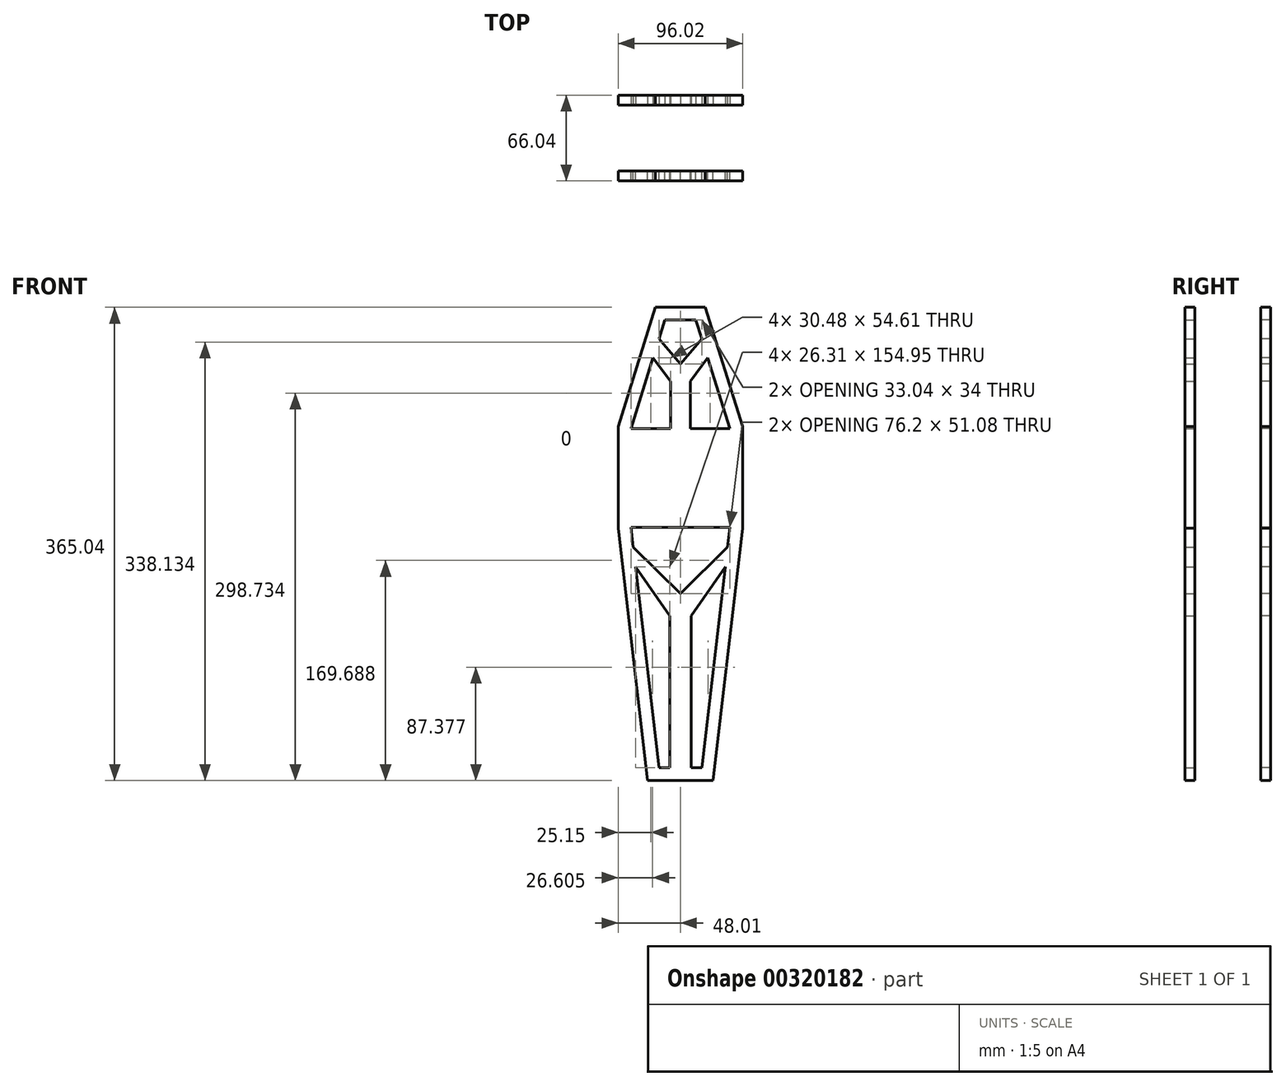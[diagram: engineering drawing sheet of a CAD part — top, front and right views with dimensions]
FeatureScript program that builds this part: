
annotation { "Feature Type Name" : "Feature", "Feature Type Description" : "" }
export const myFeature = defineFeature(function(context is Context, id is Id, definition is map)
    precondition{}
    {
        {
            var Q0;
            Q0=qCreatedBy(makeId("Front.planeOp"),FACE);
            var sketch = newSketch(context, id + "F0", { "sketchPlane" : qUnion([Q0])});
            skLineSegment(sketch, "E0.bottom", {"start": v(-38.1, 0) * mm, "end": v(38.1, 0) * mm});
            skLineSegment(sketch, "E0.top", {"start": v(-38.1, -76.2) * mm, "end": v(38.1, -76.2) * mm});
            skLineSegment(sketch, "E0.left", {"start": v(-38.1, 0) * mm, "end": v(-38.1, -76.2) * mm});
            skLineSegment(sketch, "E0.right", {"start": v(38.1, 0) * mm, "end": v(38.1, -76.2) * mm});
            skLineSegment(sketch, "E1", {"start": v(0, -38.1) * mm, "end": v(0, 83.7) * mm, "construction": true});
            skPoint(sketch, "E1.startSnap0", {"position": v(0, -76.2) * mm});
            skPoint(sketch, "E1.startSnap1", {"position": v(-38.1, -38.1) * mm});
            skPoint(sketch, "E1.endSnap0", {"position": v(0, 0) * mm});
            skLineSegment(sketch, "E2", {"start": v(0, 83.7) * mm, "end": v(-11.98, 83.7) * mm});
            skLineSegment(sketch, "E3", {"start": v(-11.98, 83.7) * mm, "end": v(0, 83.7) * mm});
            skLineSegment(sketch, "E4", {"start": v(11.98, 83.7) * mm, "end": v(0, 83.7) * mm});
            skLineSegment(sketch, "E5", {"start": v(-38.1, 0) * mm, "end": v(-11.98, 83.7) * mm});
            skLineSegment(sketch, "E6", {"start": v(38.1, 0) * mm, "end": v(11.98, 83.7) * mm});
            skLineSegment(sketch, "E7", {"start": v(0, -38.1) * mm, "end": v(0, -261.53) * mm, "construction": true});
            skLineSegment(sketch, "E8", {"start": v(0, -261.53) * mm, "end": v(-16.5, -261.53) * mm});
            skLineSegment(sketch, "E9", {"start": v(0, -261.53) * mm, "end": v(16.5, -261.53) * mm});
            skLineSegment(sketch, "E10", {"start": v(-16.5, -261.53) * mm, "end": v(-38.1, -76.2) * mm});
            skLineSegment(sketch, "E11", {"start": v(16.5, -261.53) * mm, "end": v(38.1, -76.2) * mm});
            skLineSegment(sketch, "E12", {"start": v(-7.62, 0) * mm, "end": v(-7.62, 36.5) * mm});
            skLineSegment(sketch, "E13", {"start": v(7.62, 0) * mm, "end": v(7.62, 36.5) * mm});
            skLineSegment(sketch, "E14", {"start": v(16.52, 69.16) * mm, "end": v(0, 49.7) * mm});
            skLineSegment(sketch, "E15", {"start": v(21.06, 54.6) * mm, "end": v(7.62, 36.5) * mm});
            skLineSegment(sketch, "E16", {"start": v(-21.06, 54.6) * mm, "end": v(-7.62, 36.5) * mm});
            skLineSegment(sketch, "E17", {"start": v(-16.52, 69.16) * mm, "end": v(0, 49.7) * mm});
            skLineSegment(sketch, "E18", {"start": v(0, 49.7) * mm, "end": v(-7.62, 36.5) * mm});
            skLineSegment(sketch, "E19", {"start": v(0, 49.7) * mm, "end": v(7.62, 36.5) * mm});
            skLineSegment(sketch, "E20", {"start": v(-7.62, 36.5) * mm, "end": v(7.62, 36.5) * mm});
            skLineSegment(sketch, "E21", {"start": v(-36.32, -91.44) * mm, "end": v(0, -127.28) * mm});
            skLineSegment(sketch, "E22", {"start": v(-34.56, -106.58) * mm, "end": v(-8.25, -144.45) * mm});
            skLineSegment(sketch, "E23", {"start": v(36.32, -91.44) * mm, "end": v(0, -127.28) * mm});
            skLineSegment(sketch, "E24", {"start": v(34.56, -106.58) * mm, "end": v(8.25, -144.45) * mm});
            skLineSegment(sketch, "E25", {"start": v(-8.25, -261.53) * mm, "end": v(-8.25, -144.45) * mm});
            skLineSegment(sketch, "E26", {"start": v(8.25, -261.53) * mm, "end": v(8.25, -144.45) * mm});
            skLineSegment(sketch, "E27", {"start": v(-8.25, -144.45) * mm, "end": v(0, -127.28) * mm});
            skLineSegment(sketch, "E28", {"start": v(0, -127.28) * mm, "end": v(8.25, -144.45) * mm});
            skLineSegment(sketch, "E29", {"start": v(-8.25, -144.45) * mm, "end": v(8.25, -144.45) * mm});
            skLineSegment(sketch, "E30.0", {"start": v(-48, 1.5) * mm, "end": v(-48, -76.78) * mm});
            skLineSegment(sketch, "E30.1", {"start": v(-25.32, -271.43) * mm, "end": v(-48, -76.78) * mm});
            skLineSegment(sketch, "E30.2", {"start": v(-48, 1.5) * mm, "end": v(-19.27, 93.61) * mm});
            skLineSegment(sketch, "E30.3", {"start": v(0, -271.43) * mm, "end": v(-25.32, -271.43) * mm});
            skLineSegment(sketch, "E30.4", {"start": v(0, -271.43) * mm, "end": v(25.32, -271.43) * mm});
            skLineSegment(sketch, "E30.5", {"start": v(25.32, -271.43) * mm, "end": v(48, -76.78) * mm});
            skLineSegment(sketch, "E30.6", {"start": v(-19.27, 93.61) * mm, "end": v(0, 93.61) * mm});
            skLineSegment(sketch, "E30.7", {"start": v(19.27, 93.61) * mm, "end": v(0, 93.61) * mm});
            skLineSegment(sketch, "E30.8", {"start": v(48, 1.5) * mm, "end": v(19.27, 93.61) * mm});
            skLineSegment(sketch, "E30.9", {"start": v(48, 1.5) * mm, "end": v(48, -76.78) * mm});
            skSolve(sketch);
        }
        {
            var Q0;
            Q0=qCreatedBy(makeId("Front.planeOp"),FACE);
            cPlane(context, id + "F1", {"entities" : qUnion([Q0]), "cplaneType" : CPlaneType.OFFSET, "offset" : 25.4 * mm, "oppositeDirection" : true, "width" : 152.4 * mm, "height" : 152.4 * mm});
        }
        {
            var Q0;
            Q0=makeQuery(id+"F0.imprint","IMPRINT",FACE,{"disambiguationData":[TD([[makeQuery(id+"F0.imprint","IMPRINT",EDGE,{"derivedFrom":sQuery(id+"F0.wireOp",EDGE,"E18")}),1.0]])]});
            var Q1;
            {var subQ0=sQuery(id+"F0.wireOp",EDGE,"E12");Q1=makeQuery(id+"F0.imprint","IMPRINT",FACE,{"disambiguationData":[TD([[makeQuery(id+"F0.imprint","IMPRINT",EDGE,{"derivedFrom":subQ0}),-1.0]])]});}
            var Q2;
            {var subQ0=sQuery(id+"F0.wireOp",EDGE,"E14");Q2=makeQuery(id+"F0.imprint","IMPRINT",FACE,{"disambiguationData":[TD([[makeQuery(id+"F0.imprint","IMPRINT",EDGE,{"derivedFrom":subQ0}),1.0]])]});}
            var Q3;
            {var subQ0=sQuery(id+"F0.wireOp",EDGE,"E16");Q3=makeQuery(id+"F0.imprint","IMPRINT",FACE,{"disambiguationData":[TD([[makeQuery(id+"F0.imprint","IMPRINT",EDGE,{"derivedFrom":subQ0}),1.0]])]});}
            var Q4;
            {var subQ8=sQuery(id+"F0.wireOp",EDGE,"E0.left");Q4=makeQuery(id+"F0.imprint","IMPRINT",FACE,{"disambiguationData":[TD([[makeQuery(id+"F0.imprint","IMPRINT",EDGE,{"derivedFrom":subQ8}),-1.0]])]});}
            var Q5;
            Q5=makeQuery(id+"F0.imprint","IMPRINT",FACE,{"disambiguationData":[TD([[makeQuery(id+"F0.imprint","IMPRINT",EDGE,{"derivedFrom":sQuery(id+"F0.wireOp",EDGE,"E0.top")}),1.0]])]});
            var Q6;
            {var subQ0=sQuery(id+"F0.wireOp",EDGE,"E21");Q6=makeQuery(id+"F0.imprint","IMPRINT",FACE,{"disambiguationData":[TD([[makeQuery(id+"F0.imprint","IMPRINT",EDGE,{"derivedFrom":subQ0}),-1.0]])]});}
            var Q7;
            {var subQ0=sQuery(id+"F0.wireOp",EDGE,"E23");Q7=makeQuery(id+"F0.imprint","IMPRINT",FACE,{"disambiguationData":[TD([[makeQuery(id+"F0.imprint","IMPRINT",EDGE,{"derivedFrom":subQ0}),1.0]])]});}
            var Q8;
            Q8=makeQuery(id+"F0.imprint","IMPRINT",FACE,{"disambiguationData":[TD([[makeQuery(id+"F0.imprint","IMPRINT",EDGE,{"derivedFrom":sQuery(id+"F0.wireOp",EDGE,"E27")}),-1.0]])]});
            var Q9;
            {var subQ4=sQuery(id+"F0.wireOp",EDGE,"E25");Q9=makeQuery(id+"F0.imprint","IMPRINT",FACE,{"disambiguationData":[TD([[makeQuery(id+"F0.imprint","IMPRINT",EDGE,{"derivedFrom":subQ4}),-1.0]])]});}
            extrude(context, id + "F2", {"entities" : qUnion([Q0, Q1, Q2, Q3, Q4, Q5, Q6, Q7, Q8, Q9]), "depth" : 7.62 * mm});
        }
        {
            var Q0;
            Q0=makeQuery(id+"F2.opExtrude","SWEPT_BODY",BODY,{"disambiguationData":[OSD([sQuery(id+"F0.wireOp",EDGE,"E0.bottom"),sQuery(id+"F0.wireOp",EDGE,"E0.top"),sQuery(id+"F0.wireOp",EDGE,"E3"),sQuery(id+"F0.wireOp",EDGE,"E4"),sQuery(id+"F0.wireOp",EDGE,"E5"),sQuery(id+"F0.wireOp",EDGE,"E6"),sQuery(id+"F0.wireOp",EDGE,"E8"),sQuery(id+"F0.wireOp",EDGE,"E9"),sQuery(id+"F0.wireOp",EDGE,"E10"),sQuery(id+"F0.wireOp",EDGE,"E11"),sQuery(id+"F0.wireOp",EDGE,"E12"),sQuery(id+"F0.wireOp",EDGE,"E13"),sQuery(id+"F0.wireOp",EDGE,"E14"),sQuery(id+"F0.wireOp",EDGE,"E15"),sQuery(id+"F0.wireOp",EDGE,"E16"),sQuery(id+"F0.wireOp",EDGE,"E17"),sQuery(id+"F0.wireOp",EDGE,"E21"),sQuery(id+"F0.wireOp",EDGE,"E22"),sQuery(id+"F0.wireOp",EDGE,"E23"),sQuery(id+"F0.wireOp",EDGE,"E24"),sQuery(id+"F0.wireOp",EDGE,"E25"),sQuery(id+"F0.wireOp",EDGE,"E26"),sQuery(id+"F0.wireOp",EDGE,"E30.0"),sQuery(id+"F0.wireOp",EDGE,"E30.1"),sQuery(id+"F0.wireOp",EDGE,"E30.2"),sQuery(id+"F0.wireOp",EDGE,"E30.3"),sQuery(id+"F0.wireOp",EDGE,"E30.4"),sQuery(id+"F0.wireOp",EDGE,"E30.5"),sQuery(id+"F0.wireOp",EDGE,"E30.6"),sQuery(id+"F0.wireOp",EDGE,"E30.7"),sQuery(id+"F0.wireOp",EDGE,"E30.8"),sQuery(id+"F0.wireOp",EDGE,"E30.9")])]});
            var Q1;
            Q1=qCreatedBy(id+"F1.planeOp",FACE);
            mirror(context, id + "F3", {"entities" : qUnion([Q0]), "mirrorPlane" : qUnion([Q1])});
        }
    });
